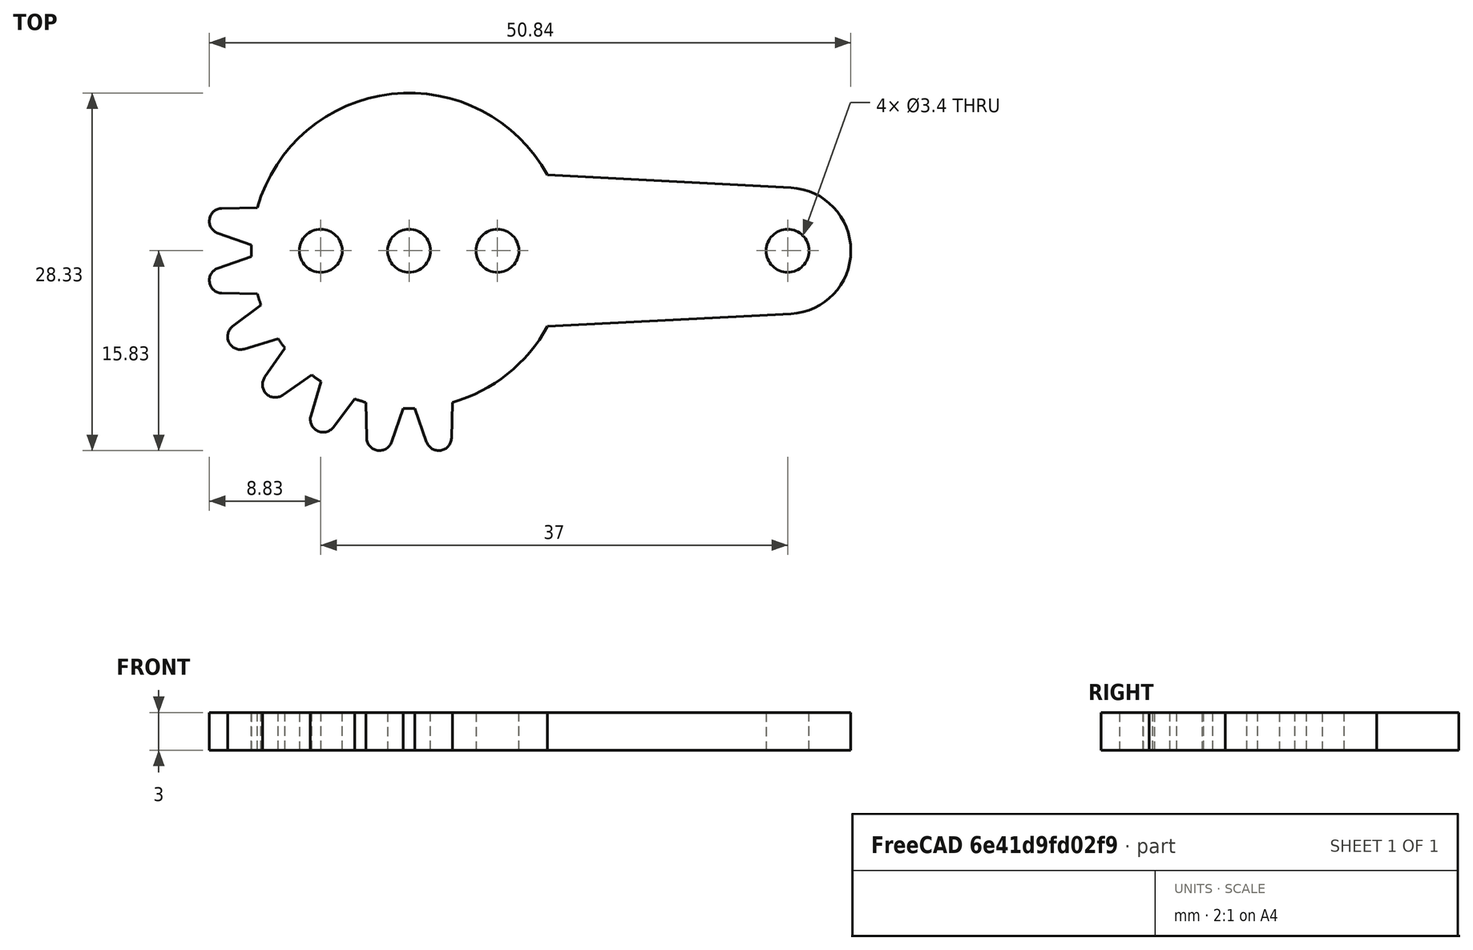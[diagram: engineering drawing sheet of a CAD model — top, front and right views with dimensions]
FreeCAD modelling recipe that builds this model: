
FCSTD DOCUMENT  (FreeCAD 0.19R24276 (Git))
Label: part3_1
License: All rights reserved
LicenseURL: http://en.wikipedia.org/wiki/All_rights_reserved
objects: Sketcher::SketchObject×1, PartDesign::Pad×1, PartDesign::Body×1
note: 4 computed .brp shape members not serialized (recipe doc carries the construction recipe); baked Part::Feature solids carry a one-line shape summary decoded from their .brp

FEATURE [Sketcher::SketchObject] Sketch
  FullyConstrained = false
  MapMode = 5
  Support = -> [XY_Plane]
  sketch-geometry (45):
    g0: Circle CenterX=0 CenterY=0 CenterZ=0 NormalX=0 NormalY=0 NormalZ=1 AngleXU=0 Radius=1.7
    g1: Circle CenterX=7 CenterY=0 CenterZ=0 NormalX=0 NormalY=0 NormalZ=1 AngleXU=0 Radius=1.7
    g2: Circle CenterX=-7 CenterY=0 CenterZ=0 NormalX=0 NormalY=0 NormalZ=1 AngleXU=0 Radius=1.7
    g3: Circle CenterX=30 CenterY=-1e-16 CenterZ=0 NormalX=0 NormalY=0 NormalZ=1 AngleXU=0 Radius=1.7
    g4: ArcOfCircle CenterX=0 CenterY=0 CenterZ=0 NormalX=0 NormalY=0 NormalZ=1 AngleXU=0 Radius=12.5 StartAngle=3.73312 EndAngle=3.8067
    g5: LineSegment StartX=10.9659 StartY=6 StartZ=0 EndX=30.2592 EndY=5 EndZ=0
    g6: ArcOfCircle CenterX=30 CenterY=-1e-16 CenterZ=0 NormalX=0 NormalY=0 NormalZ=1 AngleXU=0 Radius=5.00671 StartAngle=4.76417 EndAngle=7.8022
    g7: LineSegment StartX=30.2592 StartY=-5 StartZ=0 EndX=10.9659 EndY=-6 EndZ=0
    g8: LineSegment StartX=0 StartY=-12.5 StartZ=0 EndX=0 EndY=-6.18736 EndZ=0
    g9: LineSegment StartX=0 StartY=0 StartZ=0 EndX=-1.95543 EndY=-12.3461 EndZ=0
    g10: LineSegment StartX=0 StartY=0 StartZ=0 EndX=-5.67488 EndY=-11.1376 EndZ=0
    g11: LineSegment StartX=0 StartY=0 StartZ=0 EndX=-8.83883 EndY=-8.83883 EndZ=0
    g12: LineSegment StartX=0 StartY=0 StartZ=0 EndX=-11.1376 EndY=-5.67488 EndZ=0
    g13: LineSegment StartX=-12.0222 StartY=3.42283 StartZ=0 EndX=-14.8371 EndY=3.36243 EndZ=0
    g14: ArcOfCircle CenterX=-14.8153 CenterY=2.34652 CenterZ=0 NormalX=0 NormalY=0 NormalZ=1 AngleXU=0 Radius=1.01615 StartAngle=1.59225 EndAngle=4.37678
    g15: LineSegment StartX=-15.15 StartY=1.38706 StartZ=0 EndX=-12.4915 EndY=0.459768 EndZ=0
    g16: LineSegment StartX=-12.4915 StartY=-0.459768 StartZ=0 EndX=-15.15 EndY=-1.38706 EndZ=0
    g17: ArcOfCircle CenterX=-14.8153 CenterY=-2.34652 CenterZ=0 NormalX=0 NormalY=0 NormalZ=1 AngleXU=0 Radius=1.01615 StartAngle=1.90641 EndAngle=4.69094
    g18: LineSegment StartX=-14.8371 StartY=-3.36243 StartZ=0 EndX=-12.0222 EndY=-3.42283 EndZ=0
    g19: LineSegment StartX=-11.7381 StartY=-4.29736 StartZ=0 EndX=-13.9799 EndY=-6.00078 EndZ=0
    g20: ArcOfCircle CenterX=-13.3651 CenterY=-6.80986 CenterZ=0 NormalX=0 NormalY=0 NormalZ=1 AngleXU=0 Radius=1.01615 StartAngle=2.22057 EndAngle=5.00509
    g21: LineSegment StartX=-13.0719 StartY=-7.78279 StartZ=0 EndX=-10.3761 EndY=-6.97038 EndZ=0
    g22: LineSegment StartX=-9.83562 StartY=-7.7143 StartZ=0 EndX=-11.4413 EndY=-10.0271 EndZ=0
    g23: ArcOfCircle CenterX=-10.6066 CenterY=-10.6066 CenterZ=0 NormalX=0 NormalY=0 NormalZ=1 AngleXU=0 Radius=1.01615 StartAngle=2.53473 EndAngle=5.31925
    g24: LineSegment StartX=-10.0271 StartY=-11.4413 StartZ=0 EndX=-7.7143 EndY=-9.83562 EndZ=0
    g25: LineSegment StartX=-6.97038 StartY=-10.3761 StartZ=0 EndX=-7.78279 EndY=-13.0719 EndZ=0
    g26: ArcOfCircle CenterX=-6.80986 CenterY=-13.3651 CenterZ=0 NormalX=0 NormalY=0 NormalZ=1 AngleXU=0 Radius=1.01615 StartAngle=2.84889 EndAngle=5.63341
    g27: LineSegment StartX=-6.00078 StartY=-13.9799 StartZ=0 EndX=-4.29736 EndY=-11.7381 EndZ=0
    g28: LineSegment StartX=-3.42283 StartY=-12.0222 StartZ=0 EndX=-3.36243 EndY=-14.8371 EndZ=0
    g29: ArcOfCircle CenterX=-2.34652 CenterY=-14.8153 CenterZ=0 NormalX=0 NormalY=0 NormalZ=1 AngleXU=0 Radius=1.01615 StartAngle=3.16305 EndAngle=5.94757
    g30: LineSegment StartX=-1.38706 StartY=-15.15 StartZ=0 EndX=-0.459768 EndY=-12.4915 EndZ=0
    g31: LineSegment StartX=0.459768 StartY=-12.4915 StartZ=0 EndX=1.38706 EndY=-15.15 EndZ=0
    g32: ArcOfCircle CenterX=2.34652 CenterY=-14.8153 CenterZ=0 NormalX=0 NormalY=0 NormalZ=1 AngleXU=0 Radius=1.01615 StartAngle=3.47721 EndAngle=6.26173
    g33: LineSegment StartX=3.36243 StartY=-14.8371 StartZ=0 EndX=3.42283 EndY=-12.0222 EndZ=0
    g34: Circle CenterX=0 CenterY=0 CenterZ=0 NormalX=0 NormalY=0 NormalZ=1 AngleXU=0 Radius=12.5
    g35: ArcOfCircle CenterX=0 CenterY=0 CenterZ=0 NormalX=0 NormalY=0 NormalZ=1 AngleXU=0 Radius=12.5 StartAngle=4.04728 EndAngle=4.12086
    g36: ArcOfCircle CenterX=0 CenterY=0 CenterZ=0 NormalX=0 NormalY=0 NormalZ=1 AngleXU=0 Radius=12.5 StartAngle=4.36144 EndAngle=4.43502
    g37: ArcOfCircle CenterX=0 CenterY=0 CenterZ=0 NormalX=0 NormalY=0 NormalZ=1 AngleXU=0 Radius=12.5 StartAngle=4.6756 EndAngle=4.74918
    g38: LineSegment StartX=0 StartY=0 StartZ=0 EndX=1.95543 EndY=-12.3461 EndZ=0
    g39: ArcOfCircle CenterX=0 CenterY=0 CenterZ=0 NormalX=0 NormalY=0 NormalZ=1 AngleXU=0 Radius=12.5 StartAngle=4.98976 EndAngle=5.78253
    g40: LineSegment StartX=0 StartY=0 StartZ=0 EndX=-12.3461 EndY=-1.95543 EndZ=0
    g41: LineSegment StartX=0 StartY=0 StartZ=0 EndX=-12.3461 EndY=1.95543 EndZ=0
    g42: ArcOfCircle CenterX=0 CenterY=0 CenterZ=0 NormalX=0 NormalY=0 NormalZ=1 AngleXU=0 Radius=12.5 StartAngle=3.1048 EndAngle=3.17838
    g43: ArcOfCircle CenterX=0 CenterY=0 CenterZ=0 NormalX=0 NormalY=0 NormalZ=1 AngleXU=0 Radius=12.5 StartAngle=3.41896 EndAngle=3.49254
    g44: ArcOfCircle CenterX=0 CenterY=0 CenterZ=0 NormalX=0 NormalY=0 NormalZ=1 AngleXU=0 Radius=12.5 StartAngle=0.500655 EndAngle=2.86422
  constraints (134):
    c: Coincident(g0,g-1)
    c: PointOnObject(g1,g-1)
    c: Equal(g2,g0)
    c: Equal(g2,g1)
    c: Equal(g2,g3)
    c: Diameter(g2) = 3.4
    c: Symmetric(g2,g1,g0)
    c: DistanceX(g0,g1) = 7
    c: DistanceX(g0,g3) = 30
    c: Coincident(g4,g0)
    c: Diameter(g4) = 25
    c: PointOnObject(g5,g4)
    c: Tangent(g5,g6) = 1.5708
    c: Tangent(g6,g7) = 1.5708
    c: DistanceY(g6,g5) = 10
    c: Symmetric(g5,g6,g-1)
    c: Symmetric(g5,g7,g-1)
    c: Coincident(g6,g3)
    c: DistanceY(g7,g5) = 12
    c: PointOnObject(g8,g4)
    c: PointOnObject(g8,g-2)
    c: Vertical(g8)
    c: PointOnObject(g9,g4)
    c: PointOnObject(g10,g4)
    c: Angle(g10,g9) = 0.314159
    c: Angle(g11,g10) = 0.314159
    c: Angle(g12,g11) = 0.314159
    c: PointOnObject(g13,g4)
    c: Tangent(g13,g14) = -1.5708
    c: Tangent(g14,g15) = -1.5708
    c: Equal(g13,g15)
    c: PointOnObject(g15,g4)
    c: Distance(g14,g13) = 2
    c: Distance(g15,g13) = 3
    c: PointOnObject(g16,g4)
    c: Tangent(g16,g17) = -1.5708
    c: Tangent(g17,g18) = -1.5708
    c: Equal(g16,g18)
    c: PointOnObject(g18,g4)
    c: Distance(g16,g18) = 3
    c: Distance(g16,g17) = 2
    c: Tangent(g19,g20) = -1.5708
    c: Tangent(g20,g21) = -1.5708
    c: Equal(g19,g21)
    c: PointOnObject(g20,g12)
    c: Distance(g19,g21) = 3
    c: Distance(g20,g12) = 2.5
    c: Distance(g19,g20) = 2
    c: Tangent(g22,g23) = -1.5708
    c: Tangent(g23,g24) = -1.5708
    c: PointOnObject(g25,g4)
    c: Tangent(g25,g26) = -1.5708
    c: Tangent(g26,g27) = -1.5708
    c: PointOnObject(g28,g4)
    c: Tangent(g28,g29) = -1.5708
    c: Tangent(g29,g30) = -1.5708
    c: PointOnObject(g31,g4)
    c: Tangent(g31,g32) = -1.5708
    c: Tangent(g32,g33) = -1.5708
    c: PointOnObject(g23,g11)
    c: PointOnObject(g26,g10)
    c: PointOnObject(g29,g9)
    c: PointOnObject(g30,g4)
    c: PointOnObject(g24,g4)
    c: Equal(g22,g24)
    c: Equal(g25,g27)
    c: Equal(g28,g30)
    c: Equal(g31,g33)
    c: Distance(g22,g24) = 3
    c: Distance(g25,g27) = 3
    c: PointOnObject(g27,g4)
    c: Distance(g28,g30) = 3
    c: Distance(g31,g33) = 3
    c: Distance(g23,g11) = 2.5
    c: Distance(g26,g10) = 2.5
    c: Distance(g29,g9) = 2.5
    c: Distance(g22,g23) = 2
    c: Distance(g25,g26) = 2
    c: Distance(g28,g29) = 2
    c: Distance(g31,g32) = 2
    c: Coincident(g34,g0)
    c: PointOnObject(g31,g34)
    c: Coincident(g12,g0)
    c: Coincident(g43,g19)
    c: Coincident(g4,g21)
    c: Distance(g12,g0) = 12.5
    c: Coincident(g11,g0)
    c: Equal(g4,g35)
    c: Coincident(g4,g22)
    c: Coincident(g4,g35)
    c: PointOnObject(g35,g24)
    c: Equal(g12,g11)
    c: Coincident(g10,g0)
    c: Equal(g35,g36)
    c: PointOnObject(g35,g25)
    c: Coincident(g35,g36)
    c: PointOnObject(g36,g27)
    c: Coincident(g9,g0)
    c: Equal(g36,g37)
    c: PointOnObject(g36,g28)
    c: Coincident(g36,g37)
    c: PointOnObject(g37,g30)
    c: Coincident(g38,g0)
    c: Angle(g8,g38) = 0.15708
    c: Symmetric(g31,g33,g38)
    c: Distance(g38,g32) = 2.5
    c: Angle(g9,g8) = 0.15708
    c: Equal(g37,g39)
    c: PointOnObject(g37,g31)
    c: Coincident(g37,g39)
    c: PointOnObject(g39,g33)
    c: Equal(g12,g38)
    c: Coincident(g40,g0)
    c: PointOnObject(g40,g39)
    c: PointOnObject(g41,g34)
    c: Coincident(g41,g0)
    c: Distance(g41,g14) = 2.5
    c: Distance(g40,g17) = 2.5
    c: Equal(g39,g42)
    c: PointOnObject(g44,g13)
    c: Coincident(g39,g42)
    c: PointOnObject(g42,g15)
    c: Equal(g42,g43)
    c: PointOnObject(g42,g16)
    c: Coincident(g42,g43)
    c: PointOnObject(g43,g18)
    c: Angle(g40,g12) = 0.314159
    c: Angle(g41,g40) = 0.314159
    c: PointOnObject(g17,g40)
    c: PointOnObject(g14,g41)
    c: Equal(g39,g44)
    c: PointOnObject(g44,g5)
    c: Coincident(g39,g44)
    c: PointOnObject(g39,g7)
FEATURE [PartDesign::Pad] Pad
  Direction = (1,1,1)
  Length = 3
  Length2 = 100
  Profile = -> Sketch
  Type = 0
FEATURE [PartDesign::Body] Body
  Group = -> [Sketch,Pad]
  Origin = -> Origin
  Tip = -> Pad
